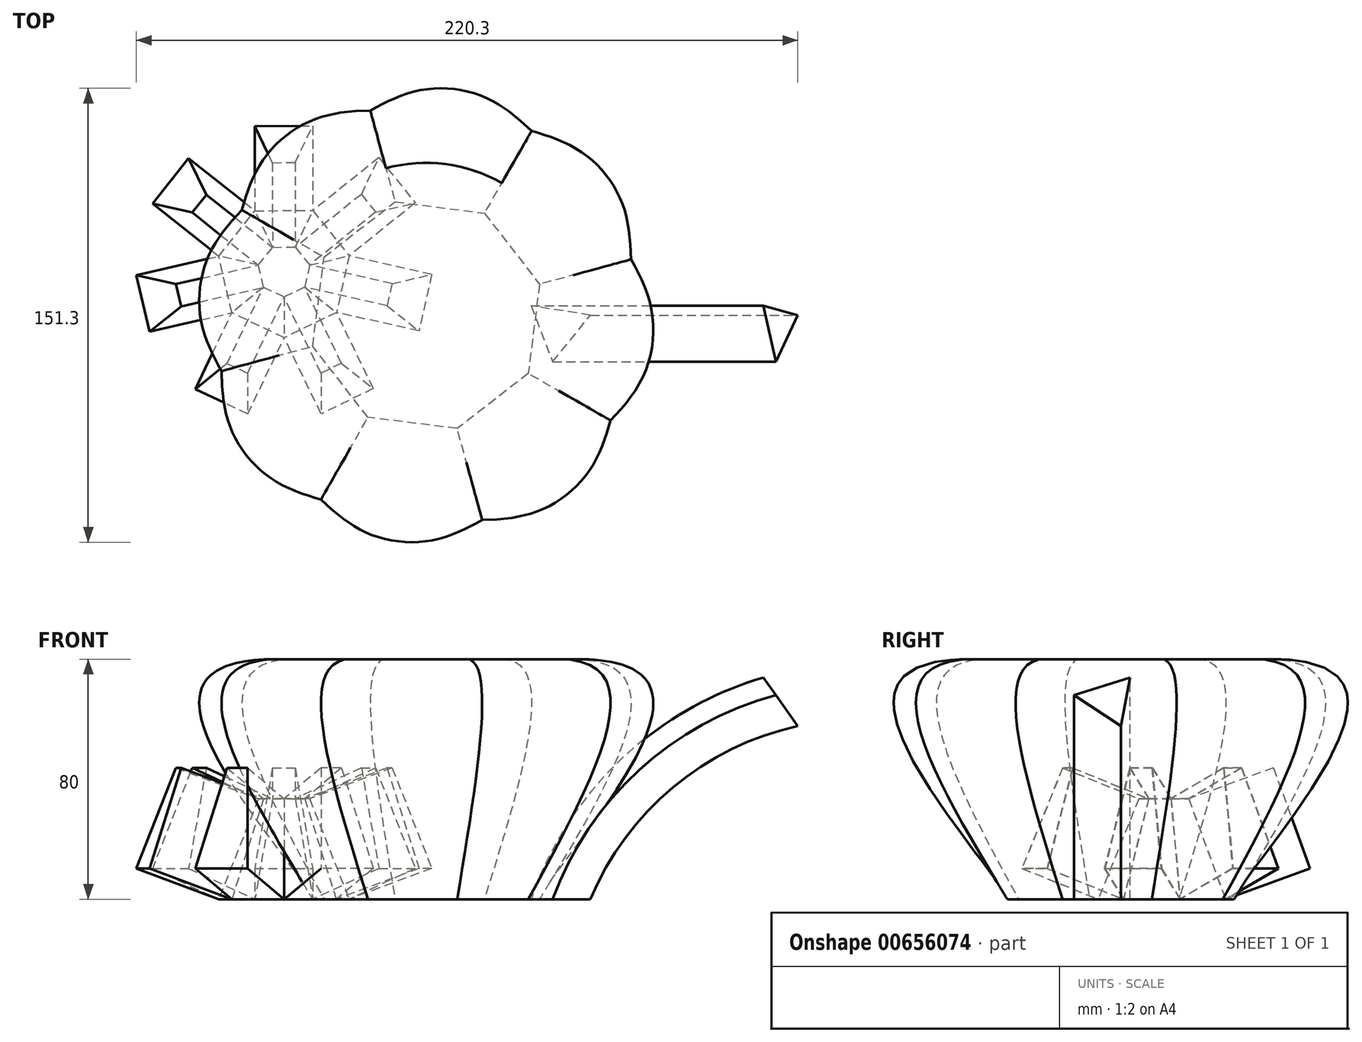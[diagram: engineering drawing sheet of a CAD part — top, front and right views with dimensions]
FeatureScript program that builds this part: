
annotation { "Feature Type Name" : "Feature", "Feature Type Description" : "" }
export const myFeature = defineFeature(function(context is Context, id is Id, definition is map)
    precondition{}
    {
        {
            var Q0;
            Q0=qCreatedBy(makeId("Top.planeOp"),FACE);
            var sketch = newSketch(context, id + "F0", { "sketchPlane" : qUnion([Q0])});
            skCircle(sketch, "E0.cCircle", {"center": v(-102.06, 14.78) * mm, "radius": 20.08 * mm, "construction": true});
            skLineSegment(sketch, "E0.0", {"start": v(-80.35, 19.8) * mm, "end": v(-84.6, 0.93) * mm});
            skLineSegment(sketch, "E0.1", {"start": v(-84.6, 0.93) * mm, "end": v(-102, -7.5) * mm});
            skLineSegment(sketch, "E0.2", {"start": v(-102, -7.5) * mm, "end": v(-119.44, 0.84) * mm});
            skLineSegment(sketch, "E0.3", {"start": v(-119.44, 0.84) * mm, "end": v(-123.8, 19.68) * mm});
            skLineSegment(sketch, "E0.4", {"start": v(-123.8, 19.68) * mm, "end": v(-111.78, 34.83) * mm});
            skLineSegment(sketch, "E0.5", {"start": v(-111.78, 34.83) * mm, "end": v(-92.44, 34.88) * mm});
            skLineSegment(sketch, "E0.6", {"start": v(-92.44, 34.88) * mm, "end": v(-80.35, 19.8) * mm});
            skPoint(sketch, "E0.0.midPoint", {"position": v(-82.47, 10.37) * mm});
            skSolve(sketch);
        }
        {
            var Q0;
            Q0 = qSketchRegion(id + "F0", true);
            extrude(context, id + "F1", {"entities" : qUnion([Q0]), "depth" : 33.5 * mm, "offsetDistance" : 25 * mm, "hasDraft" : true, "draftAngle" : 20 * degree, "draftPullDirection" : true});
        }
        {
            var Q0;
            Q0=makeQuery(id+"F1.opExtrude","SWEPT_FACE",FACE,{"disambiguationData":[OSD([sQuery(id+"F0.wireOp",EDGE,"E0.0")])]});
            var sketch = newSketch(context, id + "F2", { "sketchPlane" : qUnion([Q0])});
            skSolve(sketch);
        }
        {
            var Q0;
            {var subQ0=sQuery(id+"F0.wireOp",EDGE,"E0.0");Q0=makeQuery(id+"F2.imprint","IMPRINT",FACE,{"disambiguationData":[TD([[makeQuery(id+"F2.imprint","IMPRINT",EDGE,{"derivedFrom":makeQuery(id+"F1.opExtrude","CAP_EDGE",EDGE,{"disambiguationData":[OSD([subQ0])],"isStart":true})}),-1.0]])]});}
            extrude(context, id + "F3", {"entities" : qUnion([Q0]), "operationType" : NewBodyOperationType.ADD, "depth" : 30 * mm, "offsetDistance" : 25 * mm});
        }
        {
            var Q0;
            Q0=makeQuery(id+"F1.opExtrude","SWEPT_FACE",FACE,{"disambiguationData":[OSD([sQuery(id+"F0.wireOp",EDGE,"E0.1")])]});
            extrude(context, id + "F4", {"entities" : qUnion([Q0]), "operationType" : NewBodyOperationType.ADD, "depth" : 30 * mm, "offsetDistance" : 25 * mm});
        }
        {
            var Q0;
            Q0=makeQuery(id+"F1.opExtrude","SWEPT_FACE",FACE,{"disambiguationData":[OSD([sQuery(id+"F0.wireOp",EDGE,"E0.2")])]});
            extrude(context, id + "F5", {"entities" : qUnion([Q0]), "operationType" : NewBodyOperationType.ADD, "depth" : 30 * mm, "offsetDistance" : 25 * mm});
        }
        {
            var Q0;
            Q0=makeQuery(id+"F1.opExtrude","SWEPT_FACE",FACE,{"disambiguationData":[OSD([sQuery(id+"F0.wireOp",EDGE,"E0.3")])]});
            extrude(context, id + "F6", {"entities" : qUnion([Q0]), "operationType" : NewBodyOperationType.ADD, "depth" : 30 * mm, "offsetDistance" : 25 * mm});
        }
        {
            var Q0;
            Q0=makeQuery(id+"F1.opExtrude","SWEPT_FACE",FACE,{"disambiguationData":[OSD([sQuery(id+"F0.wireOp",EDGE,"E0.4")])]});
            extrude(context, id + "F7", {"entities" : qUnion([Q0]), "operationType" : NewBodyOperationType.ADD, "depth" : 30 * mm, "offsetDistance" : 25 * mm});
        }
        {
            var Q0;
            Q0=makeQuery(id+"F1.opExtrude","SWEPT_FACE",FACE,{"disambiguationData":[OSD([sQuery(id+"F0.wireOp",EDGE,"E0.5")])]});
            extrude(context, id + "F8", {"entities" : qUnion([Q0]), "operationType" : NewBodyOperationType.ADD, "depth" : 30 * mm, "offsetDistance" : 25 * mm});
        }
        {
            var Q0;
            Q0=makeQuery(id+"F1.opExtrude","SWEPT_FACE",FACE,{"disambiguationData":[OSD([sQuery(id+"F0.wireOp",EDGE,"E0.6")])]});
            extrude(context, id + "F9", {"entities" : qUnion([Q0]), "operationType" : NewBodyOperationType.ADD, "depth" : 30 * mm, "offsetDistance" : 25 * mm});
        }
        {
            var Q0;
            Q0=qCreatedBy(makeId("Top.planeOp"),FACE);
            cPlane(context, id + "F10", {"entities" : qUnion([Q0]), "cplaneType" : CPlaneType.OFFSET, "offset" : 80 * mm, "width" : 150 * mm, "height" : 150 * mm});
        }
        {
            var Q0;
            Q0=qCreatedBy(id+"F10.planeOp",FACE);
            var sketch = newSketch(context, id + "F11", { "sketchPlane" : qUnion([Q0])});
            skCircle(sketch, "E1", {"center": v(-54.7, 0) * mm, "radius": 50.78 * mm});
            skSolve(sketch);
        }
        {
            var Q0;
            Q0=qCreatedBy(makeId("Top.planeOp"),FACE);
            var sketch = newSketch(context, id + "F12", { "sketchPlane" : qUnion([Q0])});
            skCircle(sketch, "E2.cCircle", {"center": v(-54.72, 0) * mm, "radius": 36.2 * mm, "construction": true});
            skLineSegment(sketch, "E2.0", {"start": v(-20.69, -19.41) * mm, "end": v(-44.38, -37.79) * mm});
            skLineSegment(sketch, "E2.1", {"start": v(-44.38, -37.79) * mm, "end": v(-74.13, -34.03) * mm});
            skLineSegment(sketch, "E2.2", {"start": v(-74.13, -34.03) * mm, "end": v(-92.5, -10.34) * mm});
            skLineSegment(sketch, "E2.3", {"start": v(-92.5, -10.34) * mm, "end": v(-88.75, 19.41) * mm});
            skLineSegment(sketch, "E2.4", {"start": v(-88.75, 19.41) * mm, "end": v(-65.05, 37.79) * mm});
            skLineSegment(sketch, "E2.5", {"start": v(-65.05, 37.79) * mm, "end": v(-35.3, 34.03) * mm});
            skLineSegment(sketch, "E2.6", {"start": v(-35.3, 34.03) * mm, "end": v(-16.93, 10.34) * mm});
            skLineSegment(sketch, "E2.7", {"start": v(-16.93, 10.34) * mm, "end": v(-20.69, -19.41) * mm});
            skPoint(sketch, "E2.0.midPoint", {"position": v(-32.53, -28.6) * mm});
            skSolve(sketch);
        }
        {
            var Q0;
            Q0=makeQuery(id+"F11.imprint","IMPRINT",FACE,{"disambiguationData":[TD([[makeQuery(id+"F11.imprint","IMPRINT",EDGE,{"derivedFrom":sQuery(id+"F11.wireOp",EDGE,"E1")}),1.0]])]});
            var Q1;
            Q1=makeQuery(id+"F12.imprint","IMPRINT",FACE,{"disambiguationData":[TD([[makeQuery(id+"F12.imprint","IMPRINT",EDGE,{"derivedFrom":sQuery(id+"F12.wireOp",EDGE,"E2.0")}),-1.0]])]});
            loft(context, id + "F13", {"startCondition" : LoftEndDerivativeType.TANGENT_TO_PROFILE, "startMagnitude" : -10, "sheetProfilesArray" : [{ "sheetProfileEntities" : qUnion([Q0]) }, { "sheetProfileEntities" : qUnion([Q1]) }]});
        }
        {
            var Q0;
            Q0=qCreatedBy(makeId("Front.planeOp"),FACE);
            var sketch = newSketch(context, id + "F14", { "sketchPlane" : qUnion([Q0])});
            skArc(sketch, "E3", {"start": v(69.04, 57.73) * mm, "mid": v(27.5, 37.27) * mm, "end": v(0, 0) * mm});
            skSolve(sketch);
        }
        {
            var Q0;
            Q0=qCreatedBy(makeId("Top.planeOp"),FACE);
            var sketch = newSketch(context, id + "F15", { "sketchPlane" : qUnion([Q0])});
            skLineSegment(sketch, "E4", {"start": v(0, 0) * mm, "end": v(-19.75, 3.15) * mm});
            skLineSegment(sketch, "E5", {"start": v(-19.75, 3.15) * mm, "end": v(-12.6, -15.53) * mm});
            skLineSegment(sketch, "E6", {"start": v(-12.6, -15.53) * mm, "end": v(0, 0) * mm});
            skSolve(sketch);
        }
        {
            var Q0;
            Q0=makeQuery(id+"F15.imprint","IMPRINT",FACE,{"disambiguationData":[TD([[makeQuery(id+"F15.imprint","IMPRINT",EDGE,{"derivedFrom":sQuery(id+"F15.wireOp",EDGE,"E4")}),1.0]])]});
            var Q1;
            Q1=sQuery(id+"F14.wireOp",EDGE,"E3");
            sweep(context, id + "F16", {"profiles" : qUnion([Q0]), "path" : qUnion([Q1])});
        }
    });
